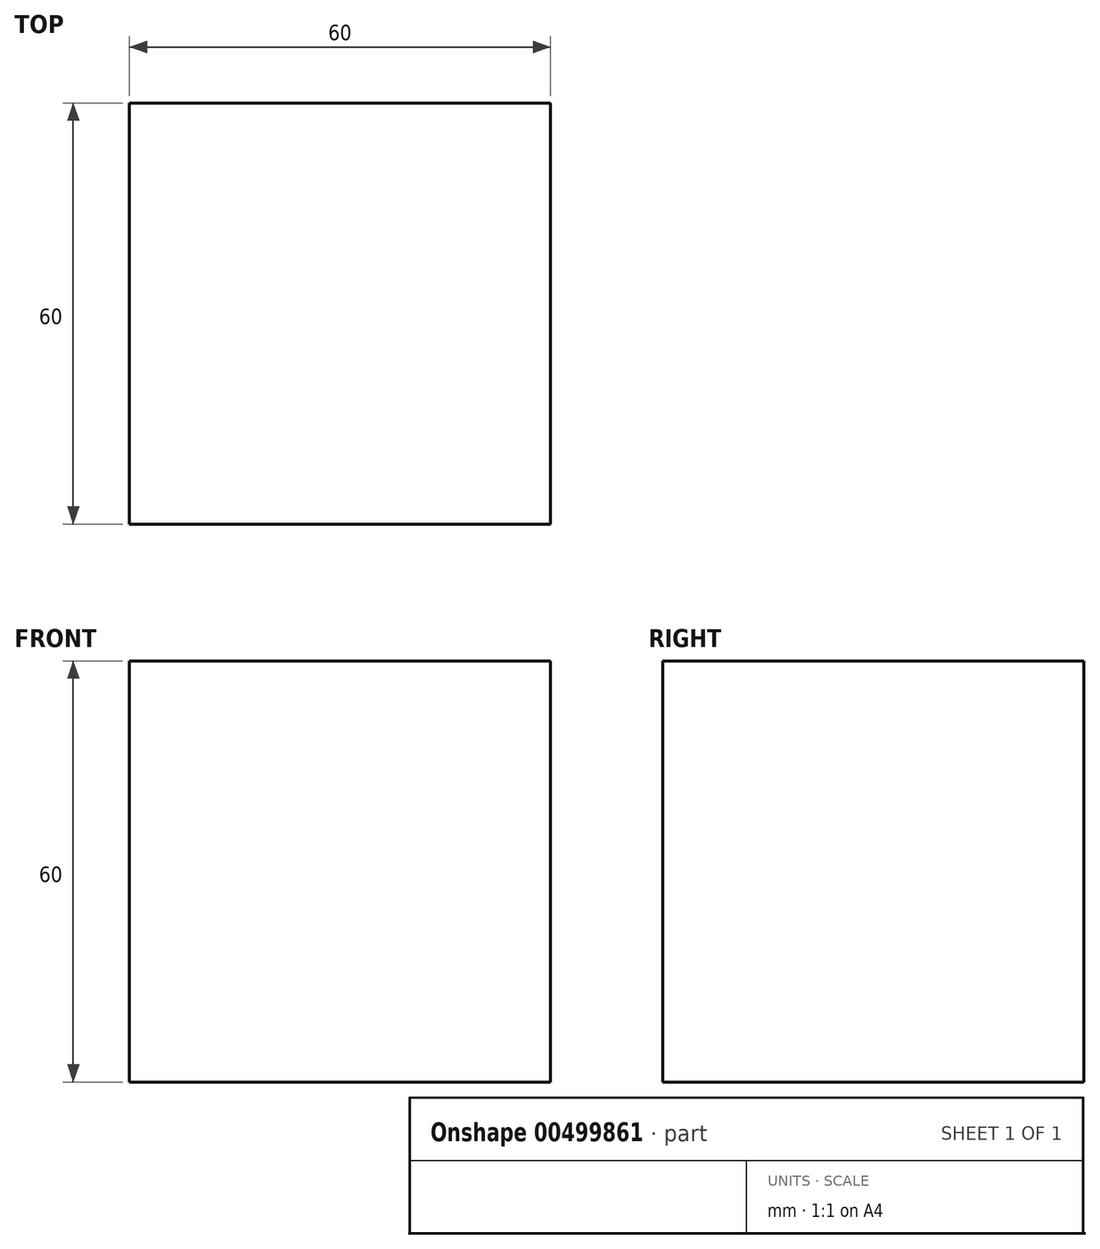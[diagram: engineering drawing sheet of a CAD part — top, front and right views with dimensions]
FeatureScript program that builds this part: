
annotation { "Feature Type Name" : "Feature", "Feature Type Description" : "" }
export const myFeature = defineFeature(function(context is Context, id is Id, definition is map)
    precondition{}
    {
        {
            var Q0;
            Q0=qCreatedBy(makeId("Top.planeOp"),FACE);
            var sketch = newSketch(context, id + "F0", { "sketchPlane" : qUnion([Q0])});
            skLineSegment(sketch, "E0.bottom", {"start": v(-4.15, 4.75) * mm, "end": v(-64.15, 4.75) * mm});
            skLineSegment(sketch, "E0.top", {"start": v(-4.15, -55.25) * mm, "end": v(-64.15, -55.25) * mm});
            skLineSegment(sketch, "E0.left", {"start": v(-4.15, 4.75) * mm, "end": v(-4.15, -55.25) * mm});
            skLineSegment(sketch, "E0.right", {"start": v(-64.15, 4.75) * mm, "end": v(-64.15, -55.25) * mm});
            skPoint(sketch, "E0.middle", {"position": v(-34.15, -25.25) * mm});
            skPoint(sketch, "E1.middle", {"position": v(-4.15, 4.75) * mm});
            skSolve(sketch);
        }
        {
            var Q0;
            Q0=makeQuery(id+"F0.imprint","IMPRINT",FACE,{"disambiguationData":[TD([[makeQuery(id+"F0.imprint","IMPRINT",EDGE,{"derivedFrom":sQuery(id+"F0.wireOp",EDGE,"E0.bottom")}),1.0]])]});
            extrude(context, id + "F1", {"entities" : qUnion([Q0]), "depth" : 60 * mm});
        }
    });
